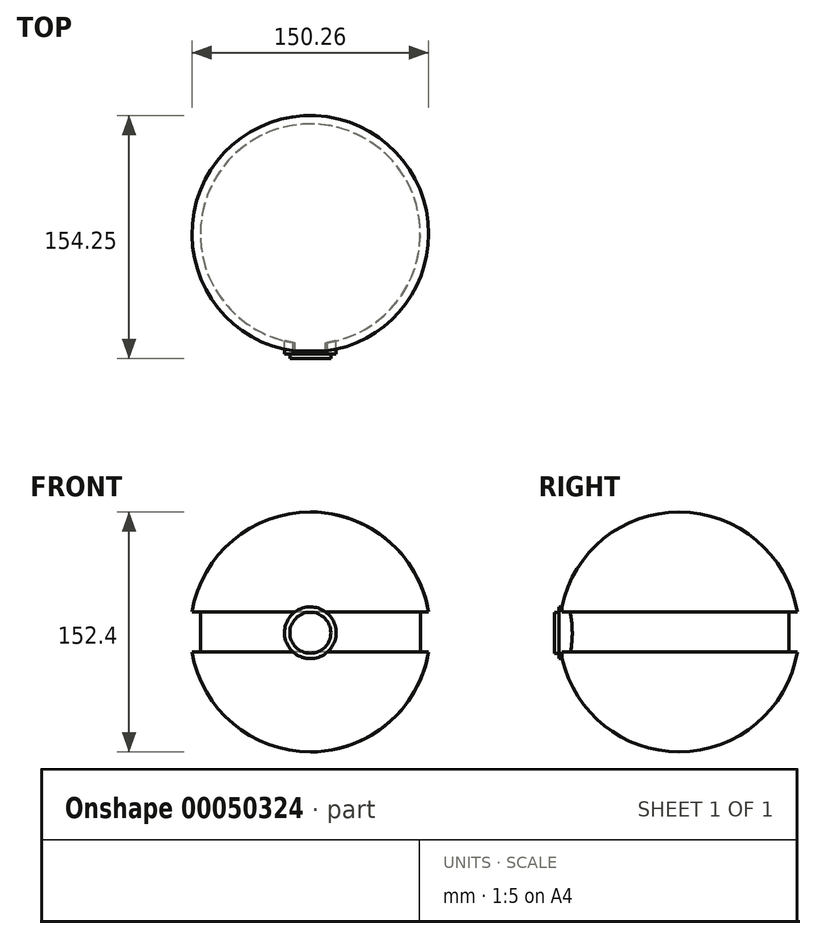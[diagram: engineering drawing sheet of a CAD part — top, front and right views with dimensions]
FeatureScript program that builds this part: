
annotation { "Feature Type Name" : "Feature", "Feature Type Description" : "" }
export const myFeature = defineFeature(function(context is Context, id is Id, definition is map)
    precondition{}
    {
        {
            var Q0;
            Q0=qCreatedBy(makeId("Front.planeOp"),FACE);
            var sketch = newSketch(context, id + "F0", { "sketchPlane" : qUnion([Q0])});
            skPoint(sketch, "E0", {"position": v(0, 152.4) * mm});
            skLineSegment(sketch, "E1", {"start": v(0, 152.4) * mm, "end": v(0, 0) * mm});
            skPoint(sketch, "E2", {"position": v(0, 76.2) * mm});
            skPoint(sketch, "E3", {"position": v(76.2, 76.2) * mm});
            skArc(sketch, "E4", {"start": v(0, 0) * mm, "mid": v(49.19, 18) * mm, "end": v(75.13, 63.5) * mm});
            skPoint(sketch, "E5", {"position": v(76.2, 88.9) * mm});
            skPoint(sketch, "E6", {"position": v(76.2, 63.5) * mm});
            skPoint(sketch, "E7", {"position": v(69.85, 88.9) * mm});
            skLineSegment(sketch, "E8.bottom", {"start": v(69.85, 88.9) * mm, "end": v(75.13, 88.9) * mm});
            skLineSegment(sketch, "E8.top", {"start": v(69.85, 63.5) * mm, "end": v(76.2, 63.5) * mm});
            skLineSegment(sketch, "E8.left", {"start": v(69.85, 88.9) * mm, "end": v(69.85, 63.5) * mm});
            skLineSegment(sketch, "E8.right", {"start": v(76.2, 88.9) * mm, "end": v(76.2, 63.5) * mm});
            skArc(sketch, "E9.trimOffspring", {"start": v(75.13, 88.9) * mm, "mid": v(49.19, 134.4) * mm, "end": v(0, 152.4) * mm});
            skSolve(sketch);
        }
        {
            var Q0;
            {var subQ2=sQuery(id+"F0.wireOp",EDGE,"E4");Q0=makeQuery(id+"F0.imprint","IMPRINT",FACE,{"disambiguationData":[TD([[makeQuery(id+"F0.imprint","IMPRINT",EDGE,{"derivedFrom":subQ2}),1.0]])]});}
            var Q1;
            Q1=sQuery(id+"F0.wireOp",EDGE,"E1");
            revolve(context, id + "F1", {"entities" : qUnion([Q0]), "axis" : qUnion([Q1]), "revolveType" : RevolveType.FULL});
        }
        {
            var Q0;
            Q0=qCreatedBy(makeId("Front.planeOp"),FACE);
            var sketch = newSketch(context, id + "F2", { "sketchPlane" : qUnion([Q0])});
            skPoint(sketch, "E10", {"position": v(0, 75.68) * mm});
            skCircle(sketch, "E11", {"center": v(0, 75.68) * mm, "radius": 16.41 * mm});
            skSolve(sketch);
        }
        {
            var Q0;
            Q0 = qSketchRegion(id + "F2", true);
            extrude(context, id + "F3", {"entities" : qUnion([Q0]), "operationType" : NewBodyOperationType.ADD, "depth" : 76.4 * mm});
        }
        {
            var Q0;
            Q0=makeQuery(id+"F3.opExtrude","CAP_FACE",FACE,{"disambiguationData":[OSD([sQuery(id+"F2.wireOp",EDGE,"E11")])],"isStart":false});
            var sketch = newSketch(context, id + "F4", { "sketchPlane" : qUnion([Q0])});
            skCircle(sketch, "E12", {"center": v(0, 75.68) * mm, "radius": 13.01 * mm});
            skSolve(sketch);
        }
        {
            var Q0;
            Q0 = qSketchRegion(id + "F4", true);
            extrude(context, id + "F5", {"entities" : qUnion([Q0]), "operationType" : NewBodyOperationType.ADD, "depth" : 2.72 * mm});
        }
    });
